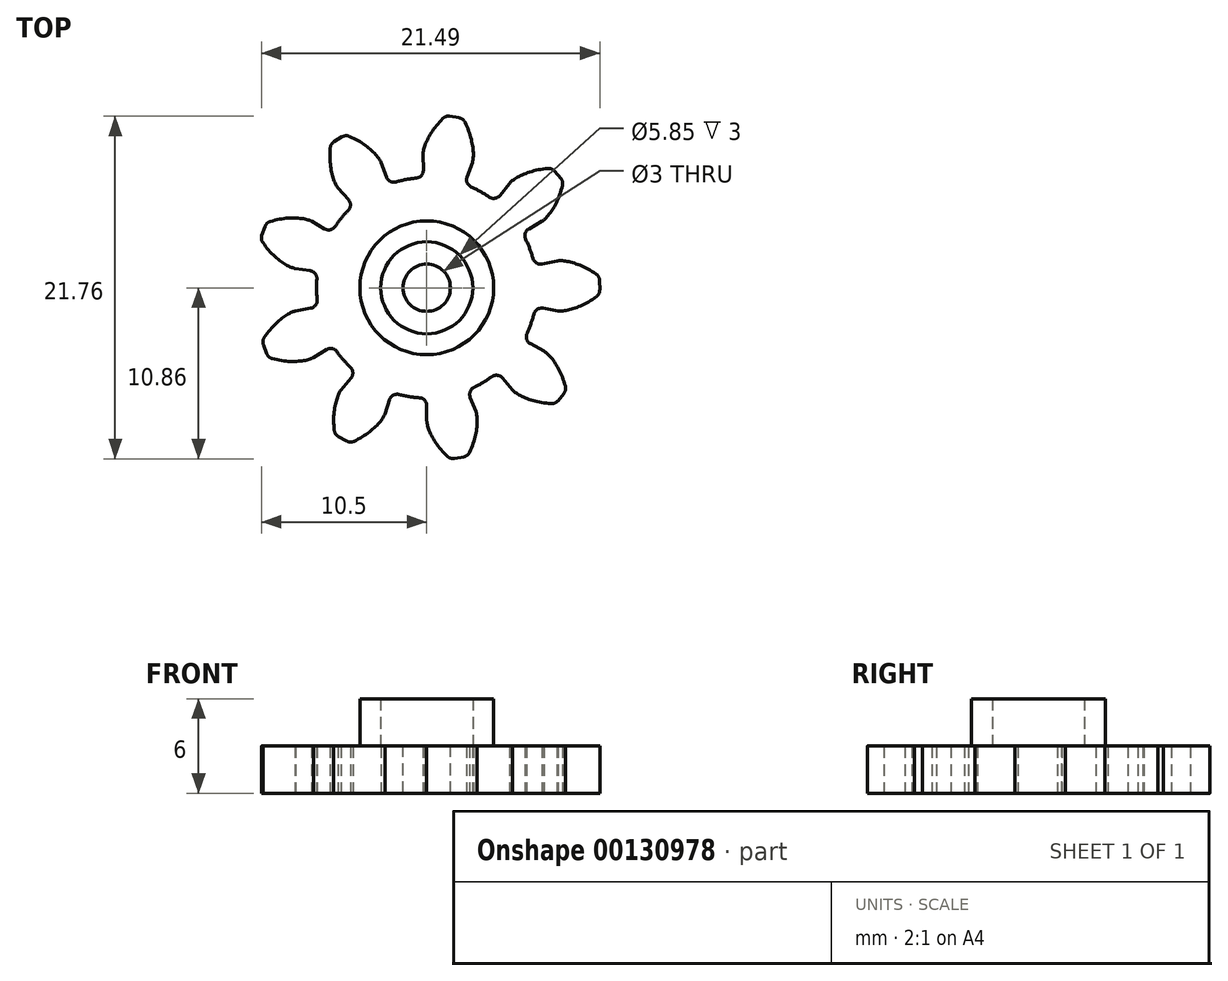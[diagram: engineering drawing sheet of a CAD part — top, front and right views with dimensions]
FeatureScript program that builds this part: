
annotation { "Feature Type Name" : "Feature", "Feature Type Description" : "" }
export const myFeature = defineFeature(function(context is Context, id is Id, definition is map)
    precondition{}
    {
        {
            var Q0;
            Q0=qCreatedBy(makeId("Top.planeOp"),FACE);
            var sketch = newSketch(context, id + "F0", { "sketchPlane" : qUnion([Q0])});
            skCircle(sketch, "E0", {"center": v(0, 0) * mm, "radius": 7 * mm});
            skCircle(sketch, "E1", {"center": v(0, 0) * mm, "radius": 9 * mm, "construction": true});
            skCircle(sketch, "E2", {"center": v(0, 0) * mm, "radius": 11 * mm, "construction": true});
            skLineSegment(sketch, "E3", {"start": v(0, 0) * mm, "end": v(0, 12.46) * mm, "construction": true});
            skLineSegment(sketch, "E4", {"start": v(0, 0) * mm, "end": v(4.57, 12.55) * mm, "construction": true});
            skLineSegment(sketch, "E5", {"start": v(0, 9) * mm, "end": v(13.43, 9) * mm, "construction": true});
            skLineSegment(sketch, "E6", {"start": v(0, 9) * mm, "end": v(16.42, 3.02) * mm, "construction": true});
            skCircle(sketch, "E7", {"center": v(0, 0) * mm, "radius": 8.46 * mm, "construction": true});
            skLineSegment(sketch, "E8", {"start": v(0, 0) * mm, "end": v(2.05, -11.65) * mm, "construction": true});
            skLineSegment(sketch, "E9", {"start": v(0, 0) * mm, "end": v(4.4, -12.1) * mm, "construction": true});
            skLineSegment(sketch, "E10", {"start": v(0, 0) * mm, "end": v(6.79, -11.76) * mm, "construction": true});
            skLineSegment(sketch, "E11", {"start": v(0, 0) * mm, "end": v(9.64, -11.49) * mm, "construction": true});
            skLineSegment(sketch, "E12", {"start": v(1.47, -8.33) * mm, "end": v(0.01, -8.59) * mm, "construction": true});
            skLineSegment(sketch, "E13", {"start": v(2.9, -7.95) * mm, "end": v(0.11, -8.96) * mm, "construction": true});
            skLineSegment(sketch, "E14", {"start": v(4.23, -7.32) * mm, "end": v(0.39, -9.54) * mm, "construction": true});
            skLineSegment(sketch, "E15", {"start": v(5.44, -6.48) * mm, "end": v(0.9, -10.28) * mm, "construction": true});
            skLineSegment(sketch, "E16", {"start": v(0, 0) * mm, "end": v(11.4, -9.56) * mm, "construction": true});
            skLineSegment(sketch, "E17", {"start": v(6.48, -5.44) * mm, "end": v(1.73, -11.1) * mm, "construction": true});
            skLineSegment(sketch, "E18", {"start": v(0, 0) * mm, "end": v(0, -13.7) * mm, "construction": true});
            skFitSpline(sketch, "E19", {"points": [v(0, -8.46) * mm, v(0.01, -8.59) * mm, v(0.11, -8.96) * mm, v(0.39, -9.54) * mm, v(0.9, -10.28) * mm, v(1.73, -11.1) * mm], "startDerivative": vector(0.06, -1.2) * mm, "endDerivative": vector(3.09, -2.87) * mm});
            skLineSegment(sketch, "E20", {"start": v(0, -8.46) * mm, "end": v(0, -6.77) * mm});
            skLineSegment(sketch, "E21", {"start": v(0, 0) * mm, "end": v(0.13, -9) * mm, "construction": true});
            skLineSegment(sketch, "E22", {"start": v(0, 0) * mm, "end": v(1.93, -10.12) * mm, "construction": true});
            skFitSpline(sketch, "E23.MirrorCS", {"points": [v(3.12, -7.86) * mm, v(3.16, -7.98) * mm, v(3.2, -8.37) * mm, v(3.16, -9.01) * mm, v(2.95, -9.89) * mm, v(2.49, -10.95) * mm], "startDerivative": vector(0.38, -1.14) * mm, "endDerivative": vector(-1.81, -3.8) * mm});
            skLineSegment(sketch, "E24.MirrorCS", {"start": v(0, 0) * mm, "end": v(5.05, -12.73) * mm});
            skLineSegment(sketch, "E25", {"start": v(1.51, -10.9) * mm, "end": v(2.61, -10.68) * mm});
            skSolve(sketch);
        }
        {
            var Q0;
            Q0 = qSketchRegion(id + "F0", true);
            extrude(context, id + "F1", {"entities" : qUnion([Q0]), "depth" : 3 * mm});
        }
        {
            var Q0;
            Q0=makeQuery(id+"F1.opExtrude","SWEPT_EDGE",EDGE,{"disambiguationData":[OSD([sQuery(id+"F0.wireOp",EDGE,"E0"),sQuery(id+"F0.wireOp",EDGE,"E20")])]});
            var Q1;
            Q1=makeQuery(id+"F1.opExtrude","SWEPT_EDGE",EDGE,{"disambiguationData":[OSD([sQuery(id+"F0.wireOp",EDGE,"E0"),sQuery(id+"F0.wireOp",EDGE,"E24.MirrorCS")])]});
            var Q2;
            Q2=makeQuery(id+"F1.opExtrude","SWEPT_EDGE",EDGE,{"disambiguationData":[OSD([sQuery(id+"F0.wireOp",EDGE,"E23.MirrorCS"),sQuery(id+"F0.wireOp",EDGE,"E25")])]});
            var Q3;
            Q3=makeQuery(id+"F1.opExtrude","SWEPT_EDGE",EDGE,{"disambiguationData":[OSD([sQuery(id+"F0.wireOp",EDGE,"E19"),sQuery(id+"F0.wireOp",EDGE,"E25")])]});
            fillet(context, id + "F2", {"entities" : qUnion([Q0, Q1, Q2, Q3]), "radius" : .5 * mm, "tangentPropagation" : true, "allowEdgeOverflow" : false});
        }
        {
            var Q0;
            Q0=qCreatedBy(makeId("Front.planeOp"),FACE);
            var sketch = newSketch(context, id + "F3", { "sketchPlane" : qUnion([Q0])});
            skLineSegment(sketch, "E26", {"start": v(0, 0) * mm, "end": v(0, 43.6) * mm, "construction": true});
            skSolve(sketch);
        }
        {
            var Q0;
            Q0=makeQuery(id+"F1.opExtrude","SWEPT_BODY",BODY,{"disambiguationData":[OSD([sQuery(id+"F0.wireOp",EDGE,"E0"),sQuery(id+"F0.wireOp",EDGE,"E19"),sQuery(id+"F0.wireOp",EDGE,"E20"),sQuery(id+"F0.wireOp",EDGE,"E23.MirrorCS"),sQuery(id+"F0.wireOp",EDGE,"E24.MirrorCS"),sQuery(id+"F0.wireOp",EDGE,"E25")])]});
            var Q1;
            Q1=sQuery(id+"F3.wireOp",EDGE,"E26");
            circularPattern(context, id + "F4", {"operationType" : NewBodyOperationType.ADD, "entities" : qUnion([Q0]), "axis" : qUnion([Q1]), "angle" : 360 / 9 * degree, "instanceCount" : 9});
        }
        {
            var Q0;
            {var subQ0=makeQuery(id+"F1.opExtrude","CAP_FACE",FACE,{"disambiguationData":[OSD([sQuery(id+"F0.wireOp",EDGE,"E0"),sQuery(id+"F0.wireOp",EDGE,"E19"),sQuery(id+"F0.wireOp",EDGE,"E20"),sQuery(id+"F0.wireOp",EDGE,"E23.MirrorCS"),sQuery(id+"F0.wireOp",EDGE,"E24.MirrorCS"),sQuery(id+"F0.wireOp",EDGE,"E25")])],"isStart":false});Q0=makeQuery(id+"F4.boolean.opBoolean","MERGE",FACE,{"derivedFrom":[subQ0,makeQuery(id+"F4.opPattern","COPY",FACE,{"derivedFrom":subQ0,"instanceName":"1"}),makeQuery(id+"F4.opPattern","COPY",FACE,{"derivedFrom":subQ0,"instanceName":"2"}),makeQuery(id+"F4.opPattern","COPY",FACE,{"derivedFrom":subQ0,"instanceName":"3"}),makeQuery(id+"F4.opPattern","COPY",FACE,{"derivedFrom":subQ0,"instanceName":"4"}),makeQuery(id+"F4.opPattern","COPY",FACE,{"derivedFrom":subQ0,"instanceName":"5"}),makeQuery(id+"F4.opPattern","COPY",FACE,{"derivedFrom":subQ0,"instanceName":"6"}),makeQuery(id+"F4.opPattern","COPY",FACE,{"derivedFrom":subQ0,"instanceName":"7"}),makeQuery(id+"F4.opPattern","COPY",FACE,{"derivedFrom":subQ0,"instanceName":"8"})]});}
            var sketch = newSketch(context, id + "F5", { "sketchPlane" : qUnion([Q0])});
            skCircle(sketch, "E27", {"center": v(0, 0) * mm, "radius": 4.25 * mm});
            skCircle(sketch, "E28", {"center": v(0, 0) * mm, "radius": 1.5 * mm});
            skCircle(sketch, "E29", {"center": v(0, 0) * mm, "radius": 2.93 * mm});
            skSolve(sketch);
        }
        {
            var Q0;
            Q0 = qSketchRegion(id + "F5", true);
            extrude(context, id + "F6", {"entities" : qUnion([Q0]), "operationType" : NewBodyOperationType.ADD, "depth" : 3 * mm});
        }
        {
            var Q0;
            Q0=makeQuery(id+"F5.imprint","IMPRINT",FACE,{"disambiguationData":[TD([[makeQuery(id+"F5.imprint","IMPRINT",EDGE,{"derivedFrom":sQuery(id+"F5.wireOp",EDGE,"E28")}),1.0]])]});
            extrude(context, id + "F7", {"entities" : qUnion([Q0]), "operationType" : NewBodyOperationType.REMOVE, "oppositeDirection" : true, "depth" : 25 * mm});
        }
    });
